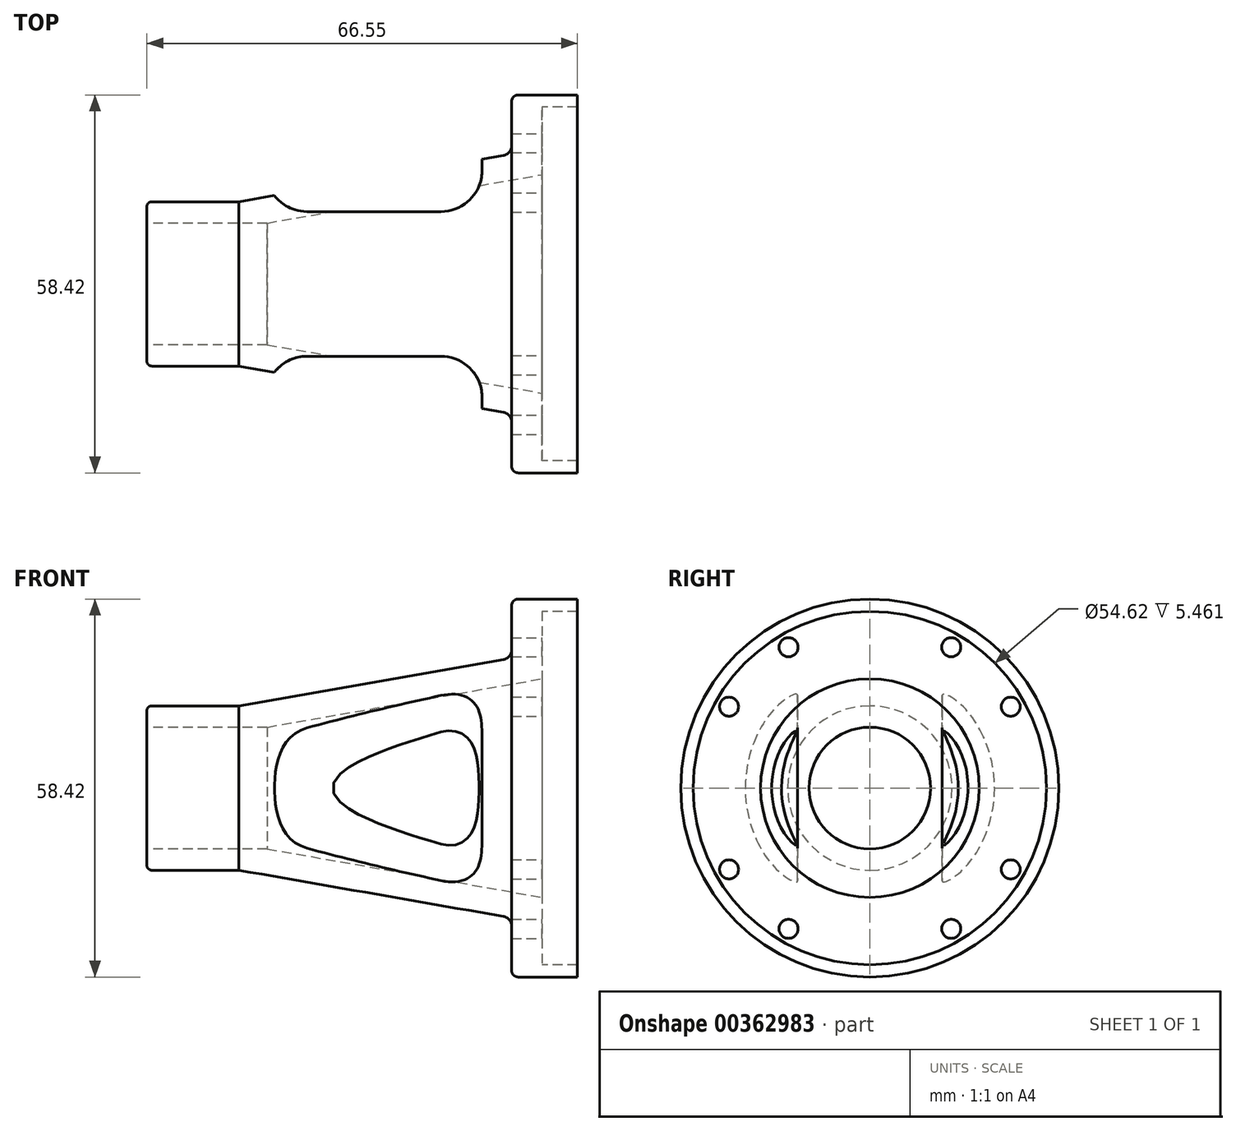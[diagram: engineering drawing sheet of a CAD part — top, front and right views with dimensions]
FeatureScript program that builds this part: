
annotation { "Feature Type Name" : "Feature", "Feature Type Description" : "" }
export const myFeature = defineFeature(function(context is Context, id is Id, definition is map)
    precondition{}
    {
        {
            var Q0;
            Q0=qCreatedBy(makeId("Front.planeOp"),FACE);
            var sketch = newSketch(context, id + "F0", { "sketchPlane" : qUnion([Q0])});
            skLineSegment(sketch, "E0", {"start": v(-39.08, 0) * mm, "end": v(38.44, 0) * mm, "construction": true});
            skLineSegment(sketch, "E1", {"start": v(-36.03, -9.4) * mm, "end": v(-17.44, -9.4) * mm});
            skLineSegment(sketch, "E2", {"start": v(-17.44, -9.4) * mm, "end": v(25.06, -16.9) * mm});
            skLineSegment(sketch, "E3", {"start": v(25.06, -16.9) * mm, "end": v(25.06, -27.31) * mm});
            skLineSegment(sketch, "E4", {"start": v(25.06, -27.31) * mm, "end": v(30.52, -27.31) * mm});
            skLineSegment(sketch, "E5", {"start": v(30.52, -27.31) * mm, "end": v(30.52, -29.21) * mm});
            skLineSegment(sketch, "E6", {"start": v(30.52, -29.21) * mm, "end": v(20.36, -29.21) * mm});
            skLineSegment(sketch, "E7", {"start": v(20.36, -29.21) * mm, "end": v(20.36, -20.07) * mm});
            skLineSegment(sketch, "E8", {"start": v(20.36, -20.07) * mm, "end": v(-21.8, -12.7) * mm});
            skLineSegment(sketch, "E9", {"start": v(-21.8, -12.7) * mm, "end": v(-36.03, -12.7) * mm});
            skLineSegment(sketch, "E10", {"start": v(-36.03, -12.7) * mm, "end": v(-36.03, -9.4) * mm});
            skLineSegment(sketch, "E11", {"start": v(20.36, -20.07) * mm, "end": v(-9.35, -20.07) * mm, "construction": true});
            skSolve(sketch);
        }
        {
            var Q0;
            Q0=makeQuery(id+"F0.imprint","IMPRINT",FACE,{"disambiguationData":[TD([[makeQuery(id+"F0.imprint","IMPRINT",EDGE,{"derivedFrom":sQuery(id+"F0.wireOp",EDGE,"E1")}),-1.0]])]});
            var Q1;
            Q1=sQuery(id+"F0.wireOp",EDGE,"E0");
            revolve(context, id + "F1", {"entities" : qUnion([Q0]), "axis" : qUnion([Q1]), "revolveType" : RevolveType.FULL});
        }
        {
            var Q0;
            Q0=makeQuery(id+"F1.opRevolve","SWEPT_EDGE",EDGE,{"disambiguationData":[OSD([sQuery(id+"F0.wireOp",EDGE,"E6"),sQuery(id+"F0.wireOp",EDGE,"E7")])]});
            fillet(context, id + "F2", {"entities" : qUnion([Q0]), "radius" : 1.02 * mm, "tangentPropagation" : true, "allowEdgeOverflow" : false});
        }
        {
            var Q0;
            Q0=makeQuery(id+"F1.opRevolve","SWEPT_EDGE",EDGE,{"disambiguationData":[OSD([sQuery(id+"F0.wireOp",EDGE,"E7"),sQuery(id+"F0.wireOp",EDGE,"E8")])]});
            fillet(context, id + "F3", {"entities" : qUnion([Q0]), "radius" : 1.52 * mm, "tangentPropagation" : true, "allowEdgeOverflow" : false});
        }
        {
            var Q0;
            Q0=makeQuery(id+"F1.opRevolve","SWEPT_EDGE",EDGE,{"disambiguationData":[OSD([sQuery(id+"F0.wireOp",EDGE,"E9"),sQuery(id+"F0.wireOp",EDGE,"E10")])]});
            fillet(context, id + "F4", {"entities" : qUnion([Q0]), "radius" : 0.76 * mm, "tangentPropagation" : true, "allowEdgeOverflow" : false});
        }
        {
            var Q0;
            Q0=qCreatedBy(makeId("Top.planeOp"),FACE);
            var sketch = newSketch(context, id + "F5", { "sketchPlane" : qUnion([Q0])});
            skLineSegment(sketch, "E12", {"start": v(20.36, 21.35) * mm, "end": v(20.36, -21.35) * mm});
            skLineSegment(sketch, "E13", {"start": v(-37.56, 0) * mm, "end": v(37.86, 0) * mm});
            skLineSegment(sketch, "E14.0", {"start": v(-11.28, -11.18) * mm, "end": v(9.43, -11.18) * mm});
            skLineSegment(sketch, "E15.0", {"start": v(-11.28, 11.18) * mm, "end": v(9.43, 11.18) * mm});
            skLineSegment(sketch, "E16.0", {"start": v(15.78, 21.35) * mm, "end": v(15.78, 17.53) * mm});
            skLineSegment(sketch, "E17", {"start": v(-17.63, 21.25) * mm, "end": v(-17.63, 17.53) * mm});
            skLineSegment(sketch, "E18", {"start": v(15.78, 21.35) * mm, "end": v(-17.63, 21.25) * mm});
            skLineSegment(sketch, "E19", {"start": v(15.78, -21.35) * mm, "end": v(-17.63, -20.18) * mm});
            skLineSegment(sketch, "E20.trimOffspring", {"start": v(-17.63, -17.53) * mm, "end": v(-17.63, -20.18) * mm});
            skLineSegment(sketch, "E21.trimOffspring", {"start": v(15.78, -17.53) * mm, "end": v(15.78, -21.35) * mm});
            skArc(sketch, "E22.filletArc", {"start": v(9.43, 11.18) * mm, "mid": v(13.93, 13.04) * mm, "end": v(15.78, 17.53) * mm});
            skArc(sketch, "E23.filletArc", {"start": v(-17.63, 17.53) * mm, "mid": v(-15.77, 13.04) * mm, "end": v(-11.28, 11.18) * mm});
            skArc(sketch, "E24.filletArc", {"start": v(-11.28, -11.18) * mm, "mid": v(-15.77, -13.04) * mm, "end": v(-17.63, -17.53) * mm});
            skArc(sketch, "E25.filletArc", {"start": v(15.78, -17.53) * mm, "mid": v(13.93, -13.04) * mm, "end": v(9.43, -11.18) * mm});
            skSolve(sketch);
        }
        {
            var Q0;
            Q0=makeQuery(id+"F5.imprint","IMPRINT",FACE,{"disambiguationData":[TD([[makeQuery(id+"F5.imprint","IMPRINT",EDGE,{"derivedFrom":sQuery(id+"F5.wireOp",EDGE,"E15.0")}),1.0]])]});
            var Q1;
            Q1=makeQuery(id+"F5.imprint","IMPRINT",FACE,{"disambiguationData":[TD([[makeQuery(id+"F5.imprint","IMPRINT",EDGE,{"derivedFrom":sQuery(id+"F5.wireOp",EDGE,"E14.0")}),-1.0]])]});
            extrude(context, id + "F6", {"entities" : qUnion([Q0, Q1]), "operationType" : NewBodyOperationType.REMOVE, "endBound" : BoundingType.SYMMETRIC, "oppositeDirection" : true, "depth" : 50.8 * mm});
        }
        {
            var Q0;
            Q0=makeQuery(id+"F1.opRevolve","SWEPT_FACE",FACE,{"disambiguationData":[OSD([sQuery(id+"F0.wireOp",EDGE,"E3")])]});
            var sketch = newSketch(context, id + "F7", { "sketchPlane" : qUnion([Q0])});
            skPoint(sketch, "E26", {"position": v(12.57, 21.77) * mm});
            skPoint(sketch, "E27", {"position": v(21.77, 12.57) * mm});
            skPoint(sketch, "E28.1.0", {"position": v(-21.77, 12.57) * mm});
            skPoint(sketch, "E28.1.1", {"position": v(-12.57, 21.77) * mm});
            skPoint(sketch, "E28.2.0", {"position": v(-12.57, -21.77) * mm});
            skPoint(sketch, "E28.2.1", {"position": v(-21.77, -12.57) * mm});
            skPoint(sketch, "E28.3.0", {"position": v(21.77, -12.57) * mm});
            skPoint(sketch, "E28.3.1", {"position": v(12.57, -21.77) * mm});
            skPoint(sketch, "E28.center", {"position": v(0, 0) * mm});
            skSolve(sketch);
        }
        {
            var Q0;
            Q0=sQuery(id+"F7.wireOp",VERTEX,"E26");
            var Q1;
            Q1=sQuery(id+"F7.wireOp",VERTEX,"E27");
            var Q2;
            Q2=sQuery(id+"F7.wireOp",VERTEX,"E28.3.0");
            var Q3;
            Q3=sQuery(id+"F7.wireOp",VERTEX,"E28.3.1");
            var Q4;
            Q4=sQuery(id+"F7.wireOp",VERTEX,"E28.2.0");
            var Q5;
            Q5=sQuery(id+"F7.wireOp",VERTEX,"E28.2.1");
            var Q6;
            Q6=sQuery(id+"F7.wireOp",VERTEX,"E28.1.0");
            var Q7;
            Q7=sQuery(id+"F7.wireOp",VERTEX,"E28.1.1");
            var Q8;
            Q8=makeQuery(id+"F1.opRevolve","SWEPT_BODY",BODY,{"disambiguationData":[OSD([sQuery(id+"F0.wireOp",EDGE,"E1"),sQuery(id+"F0.wireOp",EDGE,"E2"),sQuery(id+"F0.wireOp",EDGE,"E3"),sQuery(id+"F0.wireOp",EDGE,"E4"),sQuery(id+"F0.wireOp",EDGE,"E5"),sQuery(id+"F0.wireOp",EDGE,"E6"),sQuery(id+"F0.wireOp",EDGE,"E7"),sQuery(id+"F0.wireOp",EDGE,"E8"),sQuery(id+"F0.wireOp",EDGE,"E9"),sQuery(id+"F0.wireOp",EDGE,"E10")])]});
            hole(context, id + "F8", {"style" : HoleStyle.SIMPLE, "endStyle" : HoleEndStyle.THROUGH, "standardTappedOrClearance" : lookupTablePath({ "standard" : "ANSI", "size" : "#32 (0.12)", "type" : "Drilled" }), "standardBlindInLast" : lookupTablePath({ "standard" : "ANSI", "size" : "#32", "type" : "Drilled" }), "holeDiameter" : 2.95 * mm, "tappedDepth" : 5.4 * mm, "tapClearance" : 3, "locations" : qUnion([Q0, Q1, Q2, Q3, Q4, Q5, Q6, Q7]), "scope" : qUnion([Q8])});
        }
    });
